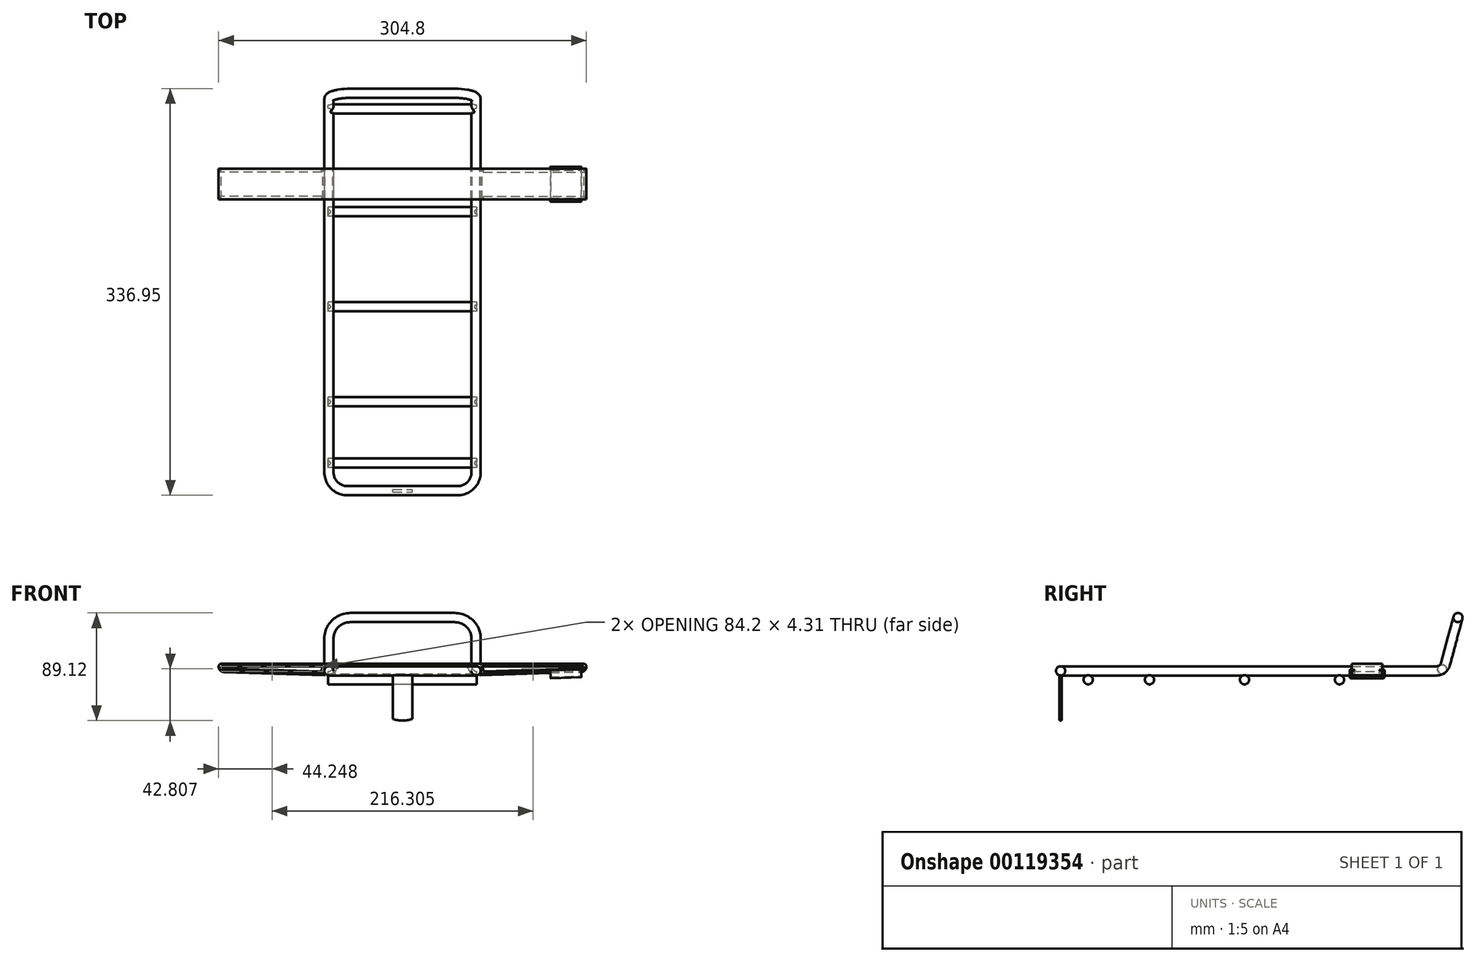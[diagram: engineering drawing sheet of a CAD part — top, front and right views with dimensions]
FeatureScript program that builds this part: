
annotation { "Feature Type Name" : "Feature", "Feature Type Description" : "" }
export const myFeature = defineFeature(function(context is Context, id is Id, definition is map)
    precondition{}
    {
        {
            var Q0;
            Q0=qCreatedBy(makeId("Right.planeOp"),FACE);
            var sketch = newSketch(context, id + "F0", { "sketchPlane" : qUnion([Q0])});
            skCircle(sketch, "E0", {"center": v(0, 0) * mm, "radius": 3.81 * mm});
            skSolve(sketch);
        }
        {
            var Q0;
            Q0=qCreatedBy(makeId("Top.planeOp"),FACE);
            var sketch = newSketch(context, id + "F1", { "sketchPlane" : qUnion([Q0])});
            skLineSegment(sketch, "E1", {"start": v(0, 0) * mm, "end": v(45.72, 0) * mm});
            skArc(sketch, "E2", {"start": v(45.72, 0) * mm, "mid": v(56.5, 4.46) * mm, "end": v(60.96, 15.24) * mm});
            skLineSegment(sketch, "E3", {"start": v(45.72, 0) * mm, "end": v(60.96, 0) * mm, "construction": true});
            skLineSegment(sketch, "E4", {"start": v(60.96, 0) * mm, "end": v(60.96, 15.24) * mm, "construction": true});
            skSolve(sketch);
        }
        {
            var Q0;
            Q0=sQuery(id+"F1.wireOp",EDGE,"E4");
            cPlane(context, id + "F2", {"entities" : qUnion([Q0]), "cplaneType" : CPlaneType.LINE_ANGLE, "offset" : 25.4 * mm, "angle" : 90 * degree, "width" : 152.4 * mm, "height" : 152.4 * mm});
        }
        {
            var Q0;
            Q0=qCreatedBy(id+"F2.planeOp",FACE);
            var sketch = newSketch(context, id + "F3", { "sketchPlane" : qUnion([Q0])});
            skLineSegment(sketch, "E5", {"start": v(15.24, 0) * mm, "end": v(311.65, 0) * mm});
            skArc(sketch, "E6", {"start": v(311.65, 0) * mm, "mid": v(316.3, 1.57) * mm, "end": v(319.01, 5.65) * mm});
            skLineSegment(sketch, "E7", {"start": v(311.65, 0) * mm, "end": v(317.5, 0) * mm, "construction": true});
            skLineSegment(sketch, "E8", {"start": v(317.5, 0) * mm, "end": v(319.01, 5.65) * mm, "construction": true});
            skSolve(sketch);
        }
        {
            var Q0;
            Q0=sQuery(id+"F3.wireOp",EDGE,"E8");
            cPlane(context, id + "F4", {"entities" : qUnion([Q0]), "cplaneType" : CPlaneType.LINE_ANGLE, "offset" : 25.4 * mm, "angle" : 90 * degree, "width" : 152.4 * mm, "height" : 152.4 * mm});
        }
        {
            var Q0;
            Q0=qCreatedBy(id+"F4.planeOp",FACE);
            var sketch = newSketch(context, id + "F5", { "sketchPlane" : qUnion([Q0])});
            skLineSegment(sketch, "E9", {"start": v(-60.96, 88.02) * mm, "end": v(-60.96, 110.12) * mm});
            skArc(sketch, "E10", {"start": v(-43.18, 127.9) * mm, "mid": v(-55.75, 122.69) * mm, "end": v(-60.96, 110.12) * mm});
            skLineSegment(sketch, "E11", {"start": v(-43.18, 127.9) * mm, "end": v(43.18, 127.9) * mm});
            skArc(sketch, "E12", {"start": v(60.96, 110.12) * mm, "mid": v(55.75, 122.69) * mm, "end": v(43.18, 127.9) * mm});
            skLineSegment(sketch, "E13", {"start": v(60.96, 110.12) * mm, "end": v(60.96, 88.02) * mm});
            skLineSegment(sketch, "E14", {"start": v(-60.96, 110.12) * mm, "end": v(-60.96, 127.9) * mm, "construction": true});
            skLineSegment(sketch, "E15", {"start": v(-60.96, 127.9) * mm, "end": v(-43.18, 127.9) * mm, "construction": true});
            skLineSegment(sketch, "E16", {"start": v(43.18, 127.9) * mm, "end": v(60.96, 127.9) * mm, "construction": true});
            skLineSegment(sketch, "E17", {"start": v(60.96, 127.9) * mm, "end": v(60.96, 110.12) * mm, "construction": true});
            skLineSegment(sketch, "E18", {"start": v(-60.96, 88.02) * mm, "end": v(60.96, 88.02) * mm, "construction": true});
            skLineSegment(sketch, "E19", {"start": v(0, 88.02) * mm, "end": v(0, 0) * mm, "construction": true});
            skSolve(sketch);
        }
        {
            var Q0;
            Q0=sQuery(id+"F5.wireOp",EDGE,"E13");
            cPlane(context, id + "F6", {"entities" : qUnion([Q0]), "cplaneType" : CPlaneType.LINE_ANGLE, "offset" : 25.4 * mm, "angle" : 0 * degree, "width" : 152.4 * mm, "height" : 152.4 * mm});
        }
        {
            var Q0;
            Q0=qCreatedBy(id+"F6.planeOp",FACE);
            var sketch = newSketch(context, id + "F7", { "sketchPlane" : qUnion([Q0])});
            skArc(sketch, "E20", {"start": v(-319.01, 5.65) * mm, "mid": v(-316.3, 1.57) * mm, "end": v(-311.65, 0) * mm});
            skLineSegment(sketch, "E21", {"start": v(-311.65, 0) * mm, "end": v(-15.24, 0) * mm});
            skSolve(sketch);
        }
        {
            var Q0;
            Q0=qCreatedBy(makeId("Top.planeOp"),FACE);
            var sketch = newSketch(context, id + "F8", { "sketchPlane" : qUnion([Q0])});
            skArc(sketch, "E22", {"start": v(-60.96, 15.24) * mm, "mid": v(-56.5, 4.46) * mm, "end": v(-45.72, 0) * mm});
            skLineSegment(sketch, "E23", {"start": v(-45.72, 0) * mm, "end": v(0, 0) * mm});
            skSolve(sketch);
        }
        {
            var Q0;
            Q0=qSketchRegion(id+"F0",true);
            var Q1;
            Q1=qConstructionFilter(qBodyType(qCreatedBy(id+"F1",EDGE),BodyType.WIRE),ConstructionObject.NO);
            var Q2;
            Q2=qConstructionFilter(qBodyType(qCreatedBy(id+"F3",EDGE),BodyType.WIRE),ConstructionObject.NO);
            var Q3;
            Q3=qConstructionFilter(qBodyType(qCreatedBy(id+"F5",EDGE),BodyType.WIRE),ConstructionObject.NO);
            var Q4;
            Q4=qConstructionFilter(qBodyType(qCreatedBy(id+"F7",EDGE),BodyType.WIRE),ConstructionObject.NO);
            var Q5;
            Q5=qConstructionFilter(qBodyType(qCreatedBy(id+"F8",EDGE),BodyType.WIRE),ConstructionObject.NO);
            sweep(context, id + "F9", {"profiles" : qUnion([Q0]), "path" : qUnion([Q1, Q2, Q3, Q4, Q5])});
        }
        {
            var Q0;
            Q0=qCreatedBy(makeId("Front.planeOp"),FACE);
            var sketch = newSketch(context, id + "F10", { "sketchPlane" : qUnion([Q0])});
            skLineSegment(sketch, "E24.bottom", {"start": v(-8, 0) * mm, "end": v(8, 0) * mm});
            skLineSegment(sketch, "E24.left", {"start": v(-8, 0) * mm, "end": v(-8, -39.85) * mm});
            skLineSegment(sketch, "E24.right", {"start": v(8, 0) * mm, "end": v(8, -39.85) * mm});
            skArc(sketch, "E25", {"start": v(-8, -39.85) * mm, "mid": v(0, -41.15) * mm, "end": v(8, -39.85) * mm});
            skSolve(sketch);
        }
        {
            var Q0;
            Q0=qSketchRegion(id+"F10",true);
            extrude(context, id + "F11", {"entities" : qUnion([Q0]), "operationType" : NewBodyOperationType.ADD, "endBound" : BoundingType.SYMMETRIC, "depth" : 2.03 * mm});
        }
        {
            var Q0;
            Q0=qCreatedBy(makeId("Right.planeOp"),FACE);
            var sketch = newSketch(context, id + "F12", { "sketchPlane" : qUnion([Q0])});
            skCircle(sketch, "E26", {"center": v(22.86, -7.37) * mm, "radius": 3.81 * mm});
            skCircle(sketch, "E27", {"center": v(73.66, -7.37) * mm, "radius": 3.81 * mm});
            skLineSegment(sketch, "E28", {"start": v(0, -3.56) * mm, "end": v(311.65, -3.56) * mm, "construction": true});
            skCircle(sketch, "E29", {"center": v(152.4, -7.37) * mm, "radius": 3.81 * mm});
            skCircle(sketch, "E30", {"center": v(231.14, -7.37) * mm, "radius": 3.81 * mm});
            skCircle(sketch, "E31", {"center": v(316.23, 1.27) * mm, "radius": 3.81 * mm});
            skSolve(sketch);
        }
        {
            var Q0;
            Q0=qSketchRegion(id+"F12",true);
            extrude(context, id + "F13", {"entities" : qUnion([Q0]), "operationType" : NewBodyOperationType.ADD, "endBound" : BoundingType.SYMMETRIC, "depth" : 123.19 * mm});
        }
        {
            var Q0;
            Q0=qCreatedBy(makeId("Front.planeOp"),FACE);
            cPlane(context, id + "F14", {"entities" : qUnion([Q0]), "cplaneType" : CPlaneType.OFFSET, "offset" : 266.7 * mm, "oppositeDirection" : true, "width" : 152.4 * mm, "height" : 152.4 * mm});
        }
        {
            var Q0;
            Q0=qCreatedBy(id+"F14.planeOp",FACE);
            var sketch = newSketch(context, id + "F15", { "sketchPlane" : qUnion([Q0])});
            skCircle(sketch, "E32", {"center": v(-60.96, 0) * mm, "radius": 3.81 * mm, "construction": true});
            skCircle(sketch, "E33", {"center": v(60.96, 0) * mm, "radius": 3.81 * mm, "construction": true});
            skLineSegment(sketch, "E34", {"start": v(60.96, 3.8) * mm, "end": v(-60.96, 3.8) * mm, "construction": true});
            skArc(sketch, "E35", {"start": v(150.11, 5.84) * mm, "mid": v(151.73, 5.17) * mm, "end": v(152.4, 3.56) * mm});
            skArc(sketch, "E36", {"start": v(152.4, 3.56) * mm, "mid": v(151.11, 0.37) * mm, "end": v(147.97, -1.01) * mm});
            skArc(sketch, "E37", {"start": v(-150.11, 5.84) * mm, "mid": v(-151.73, 5.17) * mm, "end": v(-152.4, 3.56) * mm});
            skArc(sketch, "E38", {"start": v(-152.4, 3.56) * mm, "mid": v(-151.11, 0.37) * mm, "end": v(-147.97, -1.01) * mm});
            skArc(sketch, "E39", {"start": v(64.24, -2.82) * mm, "mid": v(60.96, 3.81) * mm, "end": v(57.68, -2.82) * mm});
            skArc(sketch, "E40", {"start": v(64.24, -2.82) * mm, "mid": v(64.2, -3.36) * mm, "end": v(64.66, -3.64) * mm});
            skArc(sketch, "E41", {"start": v(57.68, -2.82) * mm, "mid": v(57.6, -3.53) * mm, "end": v(56.9, -3.46) * mm});
            skArc(sketch, "E42", {"start": v(-57.68, -2.82) * mm, "mid": v(-60.96, 3.8) * mm, "end": v(-64.24, -2.82) * mm});
            skArc(sketch, "E43", {"start": v(-57.68, -2.82) * mm, "mid": v(-57.6, -3.53) * mm, "end": v(-56.9, -3.46) * mm});
            skLineSegment(sketch, "E44", {"start": v(-147.97, -1.01) * mm, "end": v(-64.66, -3.64) * mm});
            skArc(sketch, "E45", {"start": v(-64.24, -2.82) * mm, "mid": v(-64.2, -3.36) * mm, "end": v(-64.66, -3.64) * mm});
            skLineSegment(sketch, "E46", {"start": v(64.66, -3.64) * mm, "end": v(147.97, -1.01) * mm});
            skLineSegment(sketch, "E47", {"start": v(150.11, 5.84) * mm, "end": v(0, 5.84) * mm});
            skLineSegment(sketch, "E48", {"start": v(0, 5.84) * mm, "end": v(-150.11, 5.84) * mm});
            skLineSegment(sketch, "E49", {"start": v(50.61, 3.8) * mm, "end": v(-50.61, 3.8) * mm});
            skArc(sketch, "E50", {"start": v(-56.9, -3.46) * mm, "mid": v(-56.07, -2.15) * mm, "end": v(-55.66, -0.65) * mm});
            skArc(sketch, "E51", {"start": v(55.66, -0.65) * mm, "mid": v(56.07, -2.15) * mm, "end": v(56.9, -3.46) * mm});
            skArc(sketch, "E52", {"start": v(55.66, -0.65) * mm, "mid": v(53.98, 2.53) * mm, "end": v(50.61, 3.8) * mm});
            skArc(sketch, "E53", {"start": v(-50.61, 3.8) * mm, "mid": v(-53.98, 2.53) * mm, "end": v(-55.66, -0.65) * mm});
            skLineSegment(sketch, "E54", {"start": v(64.64, -3.13) * mm, "end": v(57.28, -3.13) * mm, "construction": true});
            skLineSegment(sketch, "E55", {"start": v(-57.28, -3.13) * mm, "end": v(-64.64, -3.13) * mm, "construction": true});
            skSolve(sketch);
        }
        {
            var Q0;
            Q0=qSketchRegion(id+"F15",true);
            extrude(context, id + "F16", {"entities" : qUnion([Q0]), "depth" : 25.4 * mm});
        }
        {
            var Q0;
            Q0=makeQuery(id+"F16.opExtrude","CAP_FACE",FACE,{"disambiguationData":[OSD([sQuery(id+"F15.wireOp",EDGE,"E35"),sQuery(id+"F15.wireOp",EDGE,"E36"),sQuery(id+"F15.wireOp",EDGE,"E37"),sQuery(id+"F15.wireOp",EDGE,"E38"),sQuery(id+"F15.wireOp",EDGE,"E39"),sQuery(id+"F15.wireOp",EDGE,"E40"),sQuery(id+"F15.wireOp",EDGE,"E41"),sQuery(id+"F15.wireOp",EDGE,"E42"),sQuery(id+"F15.wireOp",EDGE,"E43"),sQuery(id+"F15.wireOp",EDGE,"E44"),sQuery(id+"F15.wireOp",EDGE,"E45"),sQuery(id+"F15.wireOp",EDGE,"E46"),sQuery(id+"F15.wireOp",EDGE,"E47"),sQuery(id+"F15.wireOp",EDGE,"E48"),sQuery(id+"F15.wireOp",EDGE,"E49"),sQuery(id+"F15.wireOp",EDGE,"E50"),sQuery(id+"F15.wireOp",EDGE,"E51"),sQuery(id+"F15.wireOp",EDGE,"E52"),sQuery(id+"F15.wireOp",EDGE,"E53")])],"isStart":true});
            var sketch = newSketch(context, id + "F17", { "sketchPlane" : qUnion([Q0])});
            skLineSegment(sketch, "E56", {"start": v(65.53, 3.8) * mm, "end": v(149.39, 3.8) * mm});
            skLineSegment(sketch, "E57", {"start": v(67.12, -0.51) * mm, "end": v(149.42, 2.08) * mm});
            skArc(sketch, "E58", {"start": v(149.39, 3.8) * mm, "mid": v(150.25, 2.96) * mm, "end": v(149.42, 2.08) * mm});
            skArc(sketch, "E59", {"start": v(67.12, -0.51) * mm, "mid": v(66.74, 1.8) * mm, "end": v(65.53, 3.8) * mm});
            skLineSegment(sketch, "E60", {"start": v(-149.39, 3.81) * mm, "end": v(-65.53, 3.81) * mm});
            skLineSegment(sketch, "E61", {"start": v(-67.12, -0.51) * mm, "end": v(-149.42, 2.08) * mm});
            skArc(sketch, "E62", {"start": v(-149.39, 3.81) * mm, "mid": v(-150.25, 2.96) * mm, "end": v(-149.42, 2.08) * mm});
            skArc(sketch, "E63", {"start": v(-65.53, 3.81) * mm, "mid": v(-66.74, 1.8) * mm, "end": v(-67.12, -0.51) * mm});
            skSolve(sketch);
        }
        {
            var Q0;
            Q0=qSketchRegion(id+"F17",true);
            extrude(context, id + "F18", {"entities" : qUnion([Q0]), "operationType" : NewBodyOperationType.REMOVE, "endBound" : BoundingType.UP_TO_NEXT, "oppositeDirection" : true, "depth" : 25.4 * mm});
        }
        {
            var Q0;
            Q0=makeQuery(id+"F16.opExtrude","SWEPT_EDGE",EDGE,{"disambiguationData":[OSD([sQuery(id+"F15.wireOp",EDGE,"E36"),sQuery(id+"F15.wireOp",EDGE,"E46")])]});
            var Q1;
            Q1=makeQuery(id+"F16.opExtrude","SWEPT_FACE",FACE,{"disambiguationData":[OSD([sQuery(id+"F15.wireOp",EDGE,"E46")])]});
            cPlane(context, id + "F19", {"entities" : qUnion([Q0, Q1]), "cplaneType" : CPlaneType.LINE_ANGLE, "offset" : 25.4 * mm, "angle" : 90 * degree, "width" : 152.4 * mm, "height" : 152.4 * mm});
        }
        {
            var Q0;
            Q0=qCreatedBy(id+"F19.planeOp",FACE);
            var sketch = newSketch(context, id + "F20", { "sketchPlane" : qUnion([Q0])});
            skLineSegment(sketch, "E64", {"start": v(241.3, -4.86) * mm, "end": v(241.3, -3.44) * mm});
            skLineSegment(sketch, "E65", {"start": v(241.3, -3.44) * mm, "end": v(243.95, -4.15) * mm});
            skLineSegment(sketch, "E66", {"start": v(243.95, -4.15) * mm, "end": v(241.3, -4.86) * mm});
            skLineSegment(sketch, "E67", {"start": v(241.3, -5.68) * mm, "end": v(241.3, -4.86) * mm, "construction": true});
            skLineSegment(sketch, "E68", {"start": v(266.7, -5.68) * mm, "end": v(266.7, -4.86) * mm, "construction": true});
            skLineSegment(sketch, "E69", {"start": v(266.7, -4.86) * mm, "end": v(266.7, -3.44) * mm});
            skLineSegment(sketch, "E70", {"start": v(266.7, -3.44) * mm, "end": v(264.05, -4.15) * mm});
            skLineSegment(sketch, "E71", {"start": v(264.05, -4.15) * mm, "end": v(266.7, -4.86) * mm});
            skSolve(sketch);
        }
        {
            var Q0;
            Q0=qSketchRegion(id+"F20",true);
            var Q1;
            Q1=makeQuery(id+"F18.boolean.opBoolean","COPY",FACE,{"derivedFrom":makeQuery(id+"F18.opExtrude","SWEPT_FACE",FACE,{"disambiguationData":[OSD([sQuery(id+"F17.wireOp",EDGE,"E63")])]})});
            var Q2;
            Q2=makeQuery(id+"F16.opExtrude","SWEPT_FACE",FACE,{"disambiguationData":[OSD([sQuery(id+"F15.wireOp",EDGE,"E36")])]});
            extrude(context, id + "F21", {"entities" : qUnion([Q0]), "operationType" : NewBodyOperationType.REMOVE, "endBound" : BoundingType.UP_TO_SURFACE, "oppositeDirection" : true, "endBoundEntityFace" : qUnion([Q1]), "depth" : 152.4 * mm, "hasSecondDirection" : true, "secondDirectionBound" : SecondDirectionBoundingType.UP_TO_SURFACE, "secondDirectionOppositeDirection" : false, "secondDirectionBoundEntityFace" : qUnion([Q2]), "secondDirectionDepth" : 25.4 * mm});
        }
        {
            var Q0;
            Q0=makeQuery(id+"F16.opExtrude","SWEPT_EDGE",EDGE,{"disambiguationData":[OSD([sQuery(id+"F15.wireOp",EDGE,"E38"),sQuery(id+"F15.wireOp",EDGE,"E44")])]});
            var Q1;
            Q1=makeQuery(id+"F16.opExtrude","SWEPT_FACE",FACE,{"disambiguationData":[OSD([sQuery(id+"F15.wireOp",EDGE,"E44")])]});
            cPlane(context, id + "F22", {"entities" : qUnion([Q0, Q1]), "cplaneType" : CPlaneType.LINE_ANGLE, "offset" : 25.4 * mm, "angle" : 90 * degree, "width" : 152.4 * mm, "height" : 152.4 * mm});
        }
        {
            var Q0;
            Q0=qCreatedBy(id+"F22.planeOp",FACE);
            var sketch = newSketch(context, id + "F23", { "sketchPlane" : qUnion([Q0])});
            skLineSegment(sketch, "E72", {"start": v(266.7, -3.44) * mm, "end": v(264.05, -4.15) * mm});
            skLineSegment(sketch, "E73", {"start": v(266.7, -3.44) * mm, "end": v(266.7, -4.86) * mm});
            skLineSegment(sketch, "E74", {"start": v(266.7, -4.86) * mm, "end": v(264.05, -4.15) * mm});
            skLineSegment(sketch, "E75", {"start": v(266.7, -4.86) * mm, "end": v(266.7, -5.68) * mm, "construction": true});
            skLineSegment(sketch, "E76", {"start": v(241.3, -5.68) * mm, "end": v(241.3, -4.86) * mm, "construction": true});
            skLineSegment(sketch, "E77", {"start": v(241.3, -4.86) * mm, "end": v(241.3, -3.44) * mm});
            skLineSegment(sketch, "E78", {"start": v(241.3, -3.44) * mm, "end": v(243.95, -4.15) * mm});
            skLineSegment(sketch, "E79", {"start": v(243.95, -4.15) * mm, "end": v(241.3, -4.86) * mm});
            skSolve(sketch);
        }
        {
            var Q0;
            Q0=qSketchRegion(id+"F23",true);
            var Q1;
            Q1=makeQuery(id+"F18.boolean.opBoolean","COPY",FACE,{"derivedFrom":makeQuery(id+"F18.opExtrude","SWEPT_FACE",FACE,{"disambiguationData":[OSD([sQuery(id+"F17.wireOp",EDGE,"E59")])]})});
            var Q2;
            Q2=makeQuery(id+"F16.opExtrude","SWEPT_FACE",FACE,{"disambiguationData":[OSD([sQuery(id+"F15.wireOp",EDGE,"E38")])]});
            extrude(context, id + "F24", {"entities" : qUnion([Q0]), "operationType" : NewBodyOperationType.REMOVE, "endBound" : BoundingType.UP_TO_SURFACE, "endBoundEntityFace" : qUnion([Q1]), "depth" : 152.4 * mm, "hasSecondDirection" : true, "secondDirectionBound" : SecondDirectionBoundingType.UP_TO_SURFACE, "secondDirectionOppositeDirection" : true, "secondDirectionBoundEntityFace" : qUnion([Q2]), "secondDirectionDepth" : 25.4 * mm});
        }
        {
            var Q0;
            Q0=qCreatedBy(id+"F19.planeOp",FACE);
            var sketch = newSketch(context, id + "F25", { "sketchPlane" : qUnion([Q0])});
            skLineSegment(sketch, "E80", {"start": v(239.52, -3.04) * mm, "end": v(243.66, -4.15) * mm});
            skLineSegment(sketch, "E81", {"start": v(243.66, -4.15) * mm, "end": v(240.8, -4.92) * mm});
            skLineSegment(sketch, "E82", {"start": v(240.8, -4.92) * mm, "end": v(240.8, -8.72) * mm});
            skLineSegment(sketch, "E83", {"start": v(267.2, -8.72) * mm, "end": v(267.2, -4.92) * mm});
            skLineSegment(sketch, "E84", {"start": v(267.2, -4.92) * mm, "end": v(264.34, -4.15) * mm});
            skLineSegment(sketch, "E85", {"start": v(264.34, -4.15) * mm, "end": v(268.48, -3.04) * mm});
            skLineSegment(sketch, "E86", {"start": v(268.48, -3.04) * mm, "end": v(268.48, -10) * mm});
            skLineSegment(sketch, "E87", {"start": v(268.48, -10) * mm, "end": v(239.52, -10) * mm});
            skLineSegment(sketch, "E88", {"start": v(239.52, -10) * mm, "end": v(239.52, -3.04) * mm});
            skLineSegment(sketch, "E89.top", {"start": v(240.8, -8.72) * mm, "end": v(267.2, -8.72) * mm});
            skLineSegment(sketch, "E90", {"start": v(254, -8.72) * mm, "end": v(254, -10) * mm, "construction": true});
            skLineSegment(sketch, "E91", {"start": v(266.7, -5.27) * mm, "end": v(267.2, -5.27) * mm, "construction": true});
            skLineSegment(sketch, "E92", {"start": v(240.8, -5.27) * mm, "end": v(241.3, -5.27) * mm, "construction": true});
            skLineSegment(sketch, "E93", {"start": v(267.2, -6.82) * mm, "end": v(268.48, -6.82) * mm, "construction": true});
            skLineSegment(sketch, "E94", {"start": v(241.6, -3.6) * mm, "end": v(241.61, -3.52) * mm, "construction": true});
            skLineSegment(sketch, "E95", {"start": v(242.23, -4.54) * mm, "end": v(242.25, -4.6) * mm, "construction": true});
            skLineSegment(sketch, "E96", {"start": v(265.77, -4.54) * mm, "end": v(265.75, -4.6) * mm, "construction": true});
            skLineSegment(sketch, "E97", {"start": v(266.4, -3.6) * mm, "end": v(266.39, -3.52) * mm, "construction": true});
            skSolve(sketch);
        }
        {
            var Q0;
            Q0=qSketchRegion(id+"F25",true);
            extrude(context, id + "F26", {"entities" : qUnion([Q0]), "oppositeDirection" : true, "depth" : 25.4 * mm});
        }
        {
            var Q0;
            Q0=makeQuery(id+"F26.opExtrude","SWEPT_EDGE",EDGE,{"disambiguationData":[OSD([sQuery(id+"F25.wireOp",EDGE,"E80"),sQuery(id+"F25.wireOp",EDGE,"E81")])]});
            var Q1;
            Q1=makeQuery(id+"F26.opExtrude","SWEPT_EDGE",EDGE,{"disambiguationData":[OSD([sQuery(id+"F25.wireOp",EDGE,"E84"),sQuery(id+"F25.wireOp",EDGE,"E85")])]});
            fillet(context, id + "F27", {"entities" : qUnion([Q0, Q1]), "radius" : 0.4 * mm, "tangentPropagation" : true, "allowEdgeOverflow" : false});
        }
        {
            var Q0;
            Q0=makeQuery(id+"F26.opExtrude","SWEPT_EDGE",EDGE,{"disambiguationData":[OSD([sQuery(id+"F25.wireOp",EDGE,"E81"),sQuery(id+"F25.wireOp",EDGE,"E82")])]});
            var Q1;
            Q1=makeQuery(id+"F26.opExtrude","SWEPT_EDGE",EDGE,{"disambiguationData":[OSD([sQuery(id+"F25.wireOp",EDGE,"E82"),sQuery(id+"F25.wireOp",EDGE,"E89.top")])]});
            var Q2;
            Q2=makeQuery(id+"F26.opExtrude","SWEPT_EDGE",EDGE,{"disambiguationData":[OSD([sQuery(id+"F25.wireOp",EDGE,"E83"),sQuery(id+"F25.wireOp",EDGE,"E89.top")])]});
            var Q3;
            Q3=makeQuery(id+"F26.opExtrude","SWEPT_EDGE",EDGE,{"disambiguationData":[OSD([sQuery(id+"F25.wireOp",EDGE,"E83"),sQuery(id+"F25.wireOp",EDGE,"E84")])]});
            fillet(context, id + "F28", {"entities" : qUnion([Q0, Q1, Q2, Q3]), "radius" : 0.5 * mm, "tangentPropagation" : true, "allowEdgeOverflow" : false});
        }
        {
            var Q0;
            Q0=makeQuery(id+"F26.opExtrude","SWEPT_EDGE",EDGE,{"disambiguationData":[OSD([sQuery(id+"F25.wireOp",EDGE,"E85"),sQuery(id+"F25.wireOp",EDGE,"E86")])]});
            var Q1;
            Q1=makeQuery(id+"F26.opExtrude","SWEPT_EDGE",EDGE,{"disambiguationData":[OSD([sQuery(id+"F25.wireOp",EDGE,"E86"),sQuery(id+"F25.wireOp",EDGE,"E87")])]});
            var Q2;
            Q2=makeQuery(id+"F26.opExtrude","SWEPT_EDGE",EDGE,{"disambiguationData":[OSD([sQuery(id+"F25.wireOp",EDGE,"E87"),sQuery(id+"F25.wireOp",EDGE,"E88")])]});
            var Q3;
            Q3=makeQuery(id+"F26.opExtrude","SWEPT_EDGE",EDGE,{"disambiguationData":[OSD([sQuery(id+"F25.wireOp",EDGE,"E80"),sQuery(id+"F25.wireOp",EDGE,"E88")])]});
            fillet(context, id + "F29", {"entities" : qUnion([Q0, Q1, Q2, Q3]), "radius" : 1.27 * mm, "tangentPropagation" : true, "allowEdgeOverflow" : false});
        }
        {
            var Q0;
            Q0=makeQuery(id+"F18.boolean.opBoolean","COPY",EDGE,{"derivedFrom":makeQuery(id+"F18.opExtrude","SWEPT_EDGE",EDGE,{"disambiguationData":[OSD([sQuery(id+"F17.wireOp",EDGE,"E57"),sQuery(id+"F17.wireOp",EDGE,"E59")])]})});
            var Q1;
            Q1=makeQuery(id+"F18.boolean.opBoolean","COPY",EDGE,{"derivedFrom":makeQuery(id+"F18.opExtrude","SWEPT_EDGE",EDGE,{"disambiguationData":[OSD([sQuery(id+"F17.wireOp",EDGE,"E56"),sQuery(id+"F17.wireOp",EDGE,"E59")])]})});
            var Q2;
            Q2=makeQuery(id+"F18.boolean.opBoolean","COPY",EDGE,{"derivedFrom":makeQuery(id+"F18.opExtrude","SWEPT_EDGE",EDGE,{"disambiguationData":[OSD([sQuery(id+"F17.wireOp",EDGE,"E60"),sQuery(id+"F17.wireOp",EDGE,"E63")])]})});
            var Q3;
            Q3=makeQuery(id+"F18.boolean.opBoolean","COPY",EDGE,{"derivedFrom":makeQuery(id+"F18.opExtrude","SWEPT_EDGE",EDGE,{"disambiguationData":[OSD([sQuery(id+"F17.wireOp",EDGE,"E61"),sQuery(id+"F17.wireOp",EDGE,"E63")])]})});
            fillet(context, id + "F30", {"entities" : qUnion([Q0, Q1, Q2, Q3]), "radius" : 0.5 * mm, "tangentPropagation" : true, "allowEdgeOverflow" : false});
        }
    });
